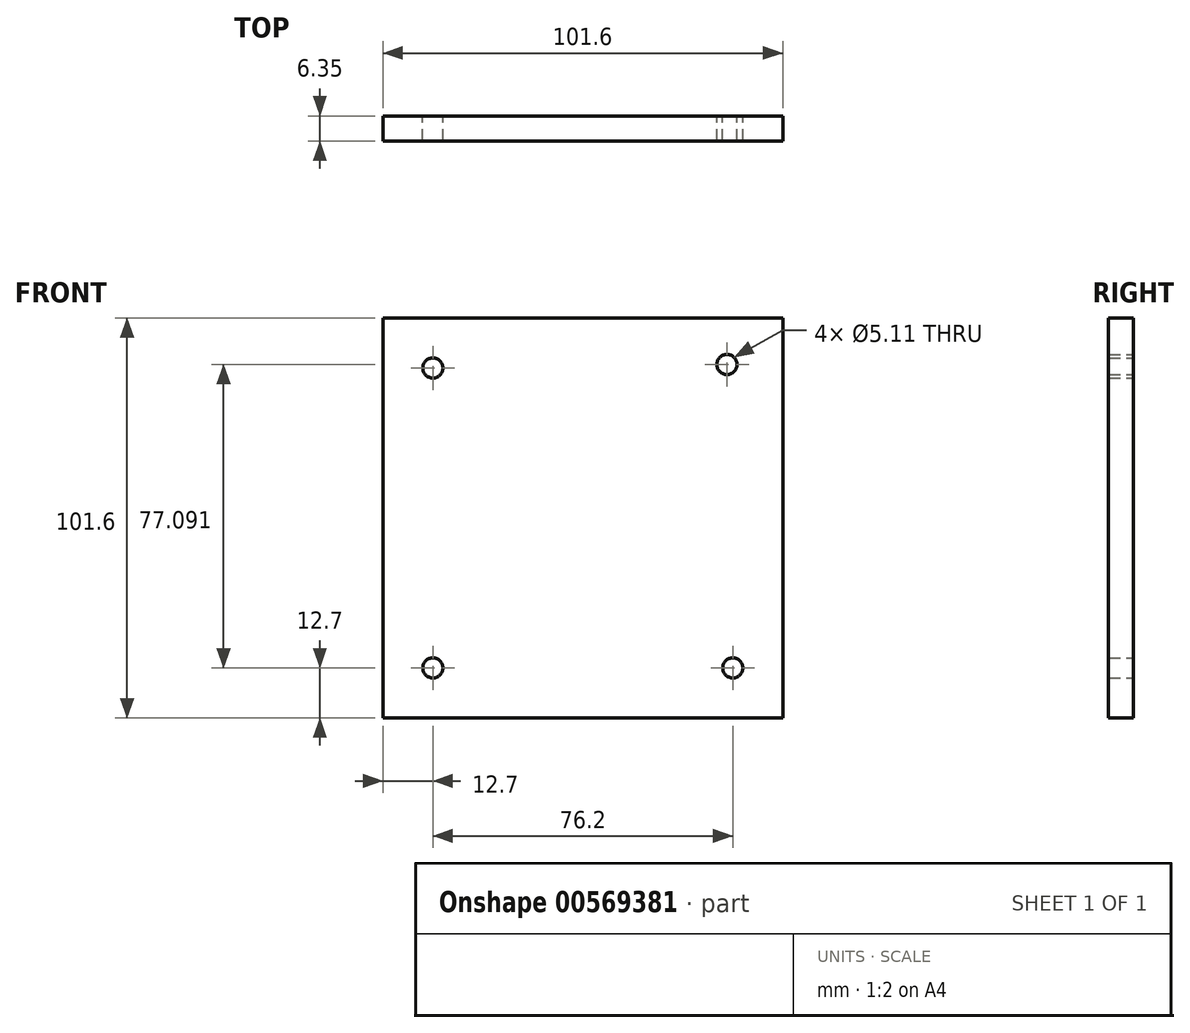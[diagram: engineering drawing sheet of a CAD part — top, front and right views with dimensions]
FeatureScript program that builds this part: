
annotation { "Feature Type Name" : "Feature", "Feature Type Description" : "" }
export const myFeature = defineFeature(function(context is Context, id is Id, definition is map)
    precondition{}
    {
        {
            var Q0;
            Q0=qCreatedBy(makeId("Front.planeOp"),FACE);
            var sketch = newSketch(context, id + "F0", { "sketchPlane" : qUnion([Q0])});
            skLineSegment(sketch, "E0.bottom", {"start": v(-50.8, 50.8) * mm, "end": v(50.8, 50.8) * mm});
            skLineSegment(sketch, "E0.top", {"start": v(-50.8, -50.8) * mm, "end": v(50.8, -50.8) * mm});
            skLineSegment(sketch, "E0.left", {"start": v(-50.8, 50.8) * mm, "end": v(-50.8, -50.8) * mm});
            skLineSegment(sketch, "E0.right", {"start": v(50.8, 50.8) * mm, "end": v(50.8, -50.8) * mm});
            skPoint(sketch, "E0.middle", {"position": v(0, 0) * mm});
            skPoint(sketch, "E1", {"position": v(-38.1, 38.1) * mm});
            skPoint(sketch, "E2", {"position": v(-38.1, -38.1) * mm});
            skPoint(sketch, "E3", {"position": v(38.1, -38.1) * mm});
            skPoint(sketch, "E4", {"position": v(36.62, 39) * mm});
            skSolve(sketch);
        }
        {
            var Q0;
            Q0=makeQuery(id+"F0.imprint","IMPRINT",FACE,{"disambiguationData":[TD([[makeQuery(id+"F0.imprint","IMPRINT",EDGE,{"derivedFrom":sQuery(id+"F0.wireOp",EDGE,"E0.bottom")}),-1.0]])]});
            extrude(context, id + "F1", {"entities" : qUnion([Q0]), "depth" : 6.35 * mm, "offsetDistance" : 25.4 * mm});
        }
        {
            var Q0;
            Q0=sQuery(id+"F0.wireOp",VERTEX,"E1");
            var Q1;
            Q1=sQuery(id+"F0.wireOp",VERTEX,"af336b0e-bca5-40aa-8357-3bc85c32982e");
            var Q2;
            Q2=sQuery(id+"F0.wireOp",VERTEX,"E3");
            var Q3;
            Q3=sQuery(id+"F0.wireOp",VERTEX,"E2");
            var Q4;
            Q4=makeQuery(id+"F1.opExtrude","SWEPT_BODY",BODY,{"disambiguationData":[OSD([sQuery(id+"F0.wireOp",EDGE,"E0.bottom"),sQuery(id+"F0.wireOp",EDGE,"E0.top"),sQuery(id+"F0.wireOp",EDGE,"E0.left"),sQuery(id+"F0.wireOp",EDGE,"E0.right")])]});
            hole(context, id + "F2", {"style" : HoleStyle.SIMPLE, "endStyle" : HoleEndStyle.THROUGH, "oppositeDirection" : true, "standardTappedOrClearance" : lookupTablePath({ "standard" : "ANSI", "engagement" : "75%", "pitch" : "20 tpi", "size" : "1/4", "type" : "Tapped" }), "standardBlindInLast" : lookupTablePath({ "standard" : "ANSI", "engagement" : "75%", "pitch" : "20 tpi", "size" : "1/4", "type" : "Tapped" }), "holeDiameter" : 5.1 * mm, "showTappedDepth" : true, "isTappedThrough" : true, "tappedDepth" : 12.7 * mm, "tapClearance" : 3, "locations" : qUnion([Q0, Q1, Q2, Q3]), "scope" : qUnion([Q4]), "majorDiameter" : 6.35 * mm});
        }
        {
            var Q0;
            Q0=sQuery(id+"F0.wireOp",VERTEX,"E4");
            var Q1;
            Q1=makeQuery(id+"F1.opExtrude","SWEPT_BODY",BODY,{"disambiguationData":[OSD([sQuery(id+"F0.wireOp",EDGE,"E0.bottom"),sQuery(id+"F0.wireOp",EDGE,"E0.top"),sQuery(id+"F0.wireOp",EDGE,"E0.left"),sQuery(id+"F0.wireOp",EDGE,"E0.right")])]});
            hole(context, id + "F3", {"style" : HoleStyle.SIMPLE, "endStyle" : HoleEndStyle.THROUGH, "oppositeDirection" : true, "standardTappedOrClearance" : lookupTablePath({ "standard" : "ANSI", "engagement" : "75%", "pitch" : "20 tpi", "size" : "1/4", "type" : "Tapped" }), "standardBlindInLast" : lookupTablePath({ "standard" : "ANSI", "engagement" : "75%", "pitch" : "20 tpi", "size" : "1/4", "type" : "Tapped" }), "holeDiameter" : 5.1 * mm, "showTappedDepth" : true, "isTappedThrough" : true, "tappedDepth" : 12.7 * mm, "tapClearance" : 3, "locations" : qUnion([Q0]), "scope" : qUnion([Q1]), "majorDiameter" : 6.35 * mm});
        }
    });
